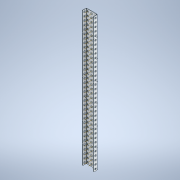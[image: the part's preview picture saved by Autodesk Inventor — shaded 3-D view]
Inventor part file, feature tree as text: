
AUTODESK INVENTOR PART (.ipt)
format: ipt  version: 2020 (Build 240168000, 168)  size: 1,404,928 bytes
history: native  units: in
note: dims shown in document units (in); Inventor stores cm internally (conversion verified against a paired STEP export)
features: other x105, plane x2, pattern_linear x1, sheet_metal_op x1
ambient origin geometry x8: Origin, YZ Plane, XZ Plane, XY Plane, X Axis, Y Axis, Z Axis, Center Point
bodies: Solid1 (feature_tree)
feature tree (109):
  other  "Work Axis1"
  pattern_linear  "Rectangular Pattern1"  Count1=35 Spacing1=0.5in
  plane  "Work Plane1"
  plane  "Work Plane2"
  other  "Work Axis2"
  other  "Work Axis3"
  other  "Work Axis4"
  other  "Work Axis5"
  other  "Work Axis6"
  other  "Work Axis7"
  other  "Work Axis8"
  other  "Work Axis9"
  other  "Work Axis10"
  other  "Work Axis11"
  other  "Work Axis12"
  other  "Work Axis13"
  other  "Work Axis14"
  other  "Work Axis15"
  other  "Work Axis16"
  other  "Work Axis17"
  other  "Work Axis18"
  other  "Work Axis19"
  other  "Work Axis20"
  other  "Work Axis21"
  other  "Work Axis22"
  other  "Work Axis23"
  other  "Work Axis24"
  other  "Work Axis25"
  other  "Work Axis26"
  other  "Work Axis27"
  other  "Work Axis28"
  other  "Work Axis29"
  other  "Work Axis30"
  other  "Work Axis31"
  other  "Work Axis32"
  other  "Work Axis33"
  other  "Work Axis34"
  other  "Work Axis35"
  other  "Work Axis36"
  other  "Work Axis37"
  other  "Work Axis38"
  other  "Work Axis39"
  other  "Work Axis40"
  other  "Work Axis41"
  other  "Work Axis42"
  other  "Work Axis43"
  other  "Work Axis44"
  other  "Work Axis45"
  other  "Work Axis46"
  other  "Work Axis47"
  other  "Work Axis48"
  other  "Work Axis49"
  other  "Work Axis50"
  other  "Work Axis51"
  other  "Work Axis52"
  other  "Work Axis53"
  other  "Work Axis54"
  other  "Work Axis55"
  other  "Work Axis56"
  other  "Work Axis57"
  other  "Work Axis58"
  other  "Work Axis59"
  other  "Work Axis60"
  other  "Work Axis61"
  other  "Work Axis62"
  other  "Work Axis63"
  other  "Work Axis64"
  other  "Work Axis65"
  other  "Work Axis66"
  other  "Work Axis67"
  other  "Work Axis68"
  other  "Work Axis69"
  other  "Work Axis70"
  other  "Work Axis71"
  other  "Work Axis72"
  other  "Work Axis73"
  other  "Work Axis74"
  other  "Work Axis75"
  other  "Work Axis76"
  other  "Work Axis77"
  other  "Work Axis78"
  other  "Work Axis79"
  other  "Work Axis80"
  other  "Work Axis81"
  other  "Work Axis82"
  other  "Work Axis83"
  other  "Work Axis84"
  other  "Work Axis85"
  other  "Work Axis86"
  other  "Work Axis87"
  other  "Work Axis88"
  other  "Work Axis89"
  other  "Work Axis90"
  other  "Work Axis91"
  other  "Work Axis92"
  other  "Work Axis93"
  other  "Work Axis94"
  other  "Work Axis95"
  other  "Work Axis96"
  other  "Work Axis97"
  other  "Work Axis98"
  other  "Work Axis99"
  other  "Work Axis100"
  other  "Work Axis101"
  other  "Work Axis102"
  other  "Work Axis103"
  other  "Work Axis104"
  other  "Work Axis105"
  sheet_metal_op  "Fold1"
